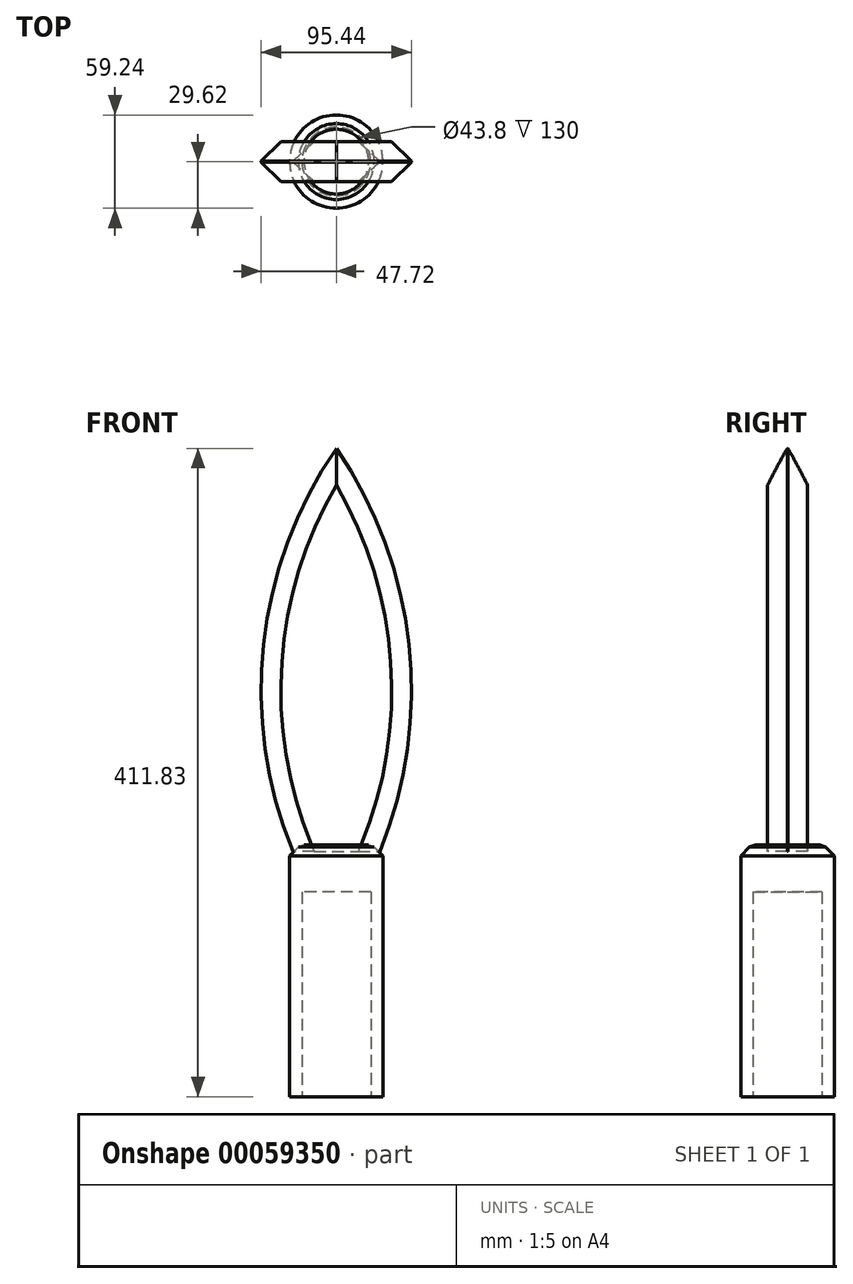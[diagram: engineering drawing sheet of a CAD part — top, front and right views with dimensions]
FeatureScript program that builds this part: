
annotation { "Feature Type Name" : "Feature", "Feature Type Description" : "" }
export const myFeature = defineFeature(function(context is Context, id is Id, definition is map)
    precondition{}
    {
        {
            var Q0;
            Q0=qCreatedBy(makeId("Top.planeOp"),FACE);
            var sketch = newSketch(context, id + "F8", { "sketchPlane" : qUnion([Q0])});
            skCircle(sketch, "E0", {"center": v(0, 0) * mm, "radius": 29.62 * mm});
            skSolve(sketch);
        }
        {
            var Q0;
            Q0 = qSketchRegion(id + "F8", true);
            extrude(context, id + "F0", {"entities" : qUnion([Q0]), "depth" : 160 * mm});
        }
        {
            var Q0;
            Q0=qCreatedBy(makeId("Front.planeOp"),FACE);
            var sketch = newSketch(context, id + "F9", { "sketchPlane" : qUnion([Q0])});
            skArc(sketch, "E1", {"start": v(27.61, 155.74) * mm, "mid": v(46.15, 287.28) * mm, "end": v(0, 411.83) * mm});
            skArc(sketch, "E2.MirrorCS", {"start": v(-27.61, 155.74) * mm, "mid": v(-46.15, 287.28) * mm, "end": v(0, 411.83) * mm});
            skLineSegment(sketch, "E3", {"start": v(-27.61, 155.74) * mm, "end": v(27.61, 155.74) * mm});
            skSolve(sketch);
        }
        {
            var Q0;
            Q0=makeQuery(id+"F9.imprint","IMPRINT",FACE,{"disambiguationData":[TD([[makeQuery(id+"F9.imprint","IMPRINT",EDGE,{"derivedFrom":sQuery(id+"F9.wireOp",EDGE,"E1")}),1.0]])]});
            extrude(context, id + "F1", {"entities" : qUnion([Q0]), "endBound" : BoundingType.SYMMETRIC, "depth" : 25.4 * mm});
        }
        {
            var Q0;
            Q0=makeQuery(id+"F1.opExtrude","CAP_EDGE",EDGE,{"disambiguationData":[OSD([sQuery(id+"F9.wireOp",EDGE,"E2.MirrorCS")])],"isStart":false});
            var Q1;
            Q1=makeQuery(id+"F1.opExtrude","CAP_EDGE",EDGE,{"disambiguationData":[OSD([sQuery(id+"F9.wireOp",EDGE,"E1")])],"isStart":false});
            var Q2;
            Q2=makeQuery(id+"F1.opExtrude","CAP_EDGE",EDGE,{"disambiguationData":[OSD([sQuery(id+"F9.wireOp",EDGE,"E2.MirrorCS")])],"isStart":true});
            var Q3;
            Q3=makeQuery(id+"F1.opExtrude","CAP_EDGE",EDGE,{"disambiguationData":[OSD([sQuery(id+"F9.wireOp",EDGE,"E1")])],"isStart":true});
            chamfer(context, id + "F2", {"entities" : qUnion([Q0, Q1, Q2, Q3]), "width" : 12.5 * mm, "tangentPropagation" : true});
        }
        {
            var Q0;
            Q0=qCreatedBy(makeId("Top.planeOp"),FACE);
            cPlane(context, id + "F3", {"entities" : qUnion([Q0]), "cplaneType" : CPlaneType.OFFSET, "offset" : 156 * mm, "width" : 150 * mm, "height" : 150 * mm});
        }
        {
            var Q0;
            Q0=makeQuery(id+"F0.opExtrude","CAP_EDGE",EDGE,{"disambiguationData":[OSD([sQuery(id+"F8.wireOp",EDGE,"E0")])],"isStart":false});
            chamfer(context, id + "F4", {"entities" : qUnion([Q0]), "width" : 7 * mm, "tangentPropagation" : true});
        }
        {
            var Q0;
            {var subQ0=sQuery(id+"F8.wireOp",EDGE,"E0");Q0=makeQuery(id+"F4.opChamfer","BLEND_EDGE",EDGE,{"blendedFrom":[makeQuery(id+"F0.opExtrude","CAP_EDGE",EDGE,{"disambiguationData":[OSD([subQ0])],"isStart":false}),makeQuery(id+"F0.opExtrude","CAP_FACE",FACE,{"disambiguationData":[OSD([subQ0])],"isStart":false})],"blendedInto":[makeQuery(id+"F0.opExtrude","CAP_FACE",FACE,{"disambiguationData":[OSD([subQ0])],"isStart":false})]});}
            chamfer(context, id + "F5", {"entities" : qUnion([Q0]), "width" : 5 * mm, "tangentPropagation" : true});
        }
        {
            var Q0;
            Q0=qCreatedBy(makeId("Top.planeOp"),FACE);
            var sketch = newSketch(context, id + "F6", { "sketchPlane" : qUnion([Q0])});
            skCircle(sketch, "E4", {"center": v(0, 0) * mm, "radius": 21.9 * mm});
            skSolve(sketch);
        }
        {
            var Q0;
            Q0 = qSketchRegion(id + "F6", true);
            extrude(context, id + "F7", {"entities" : qUnion([Q0]), "operationType" : NewBodyOperationType.REMOVE, "depth" : 130 * mm});
        }
    });
